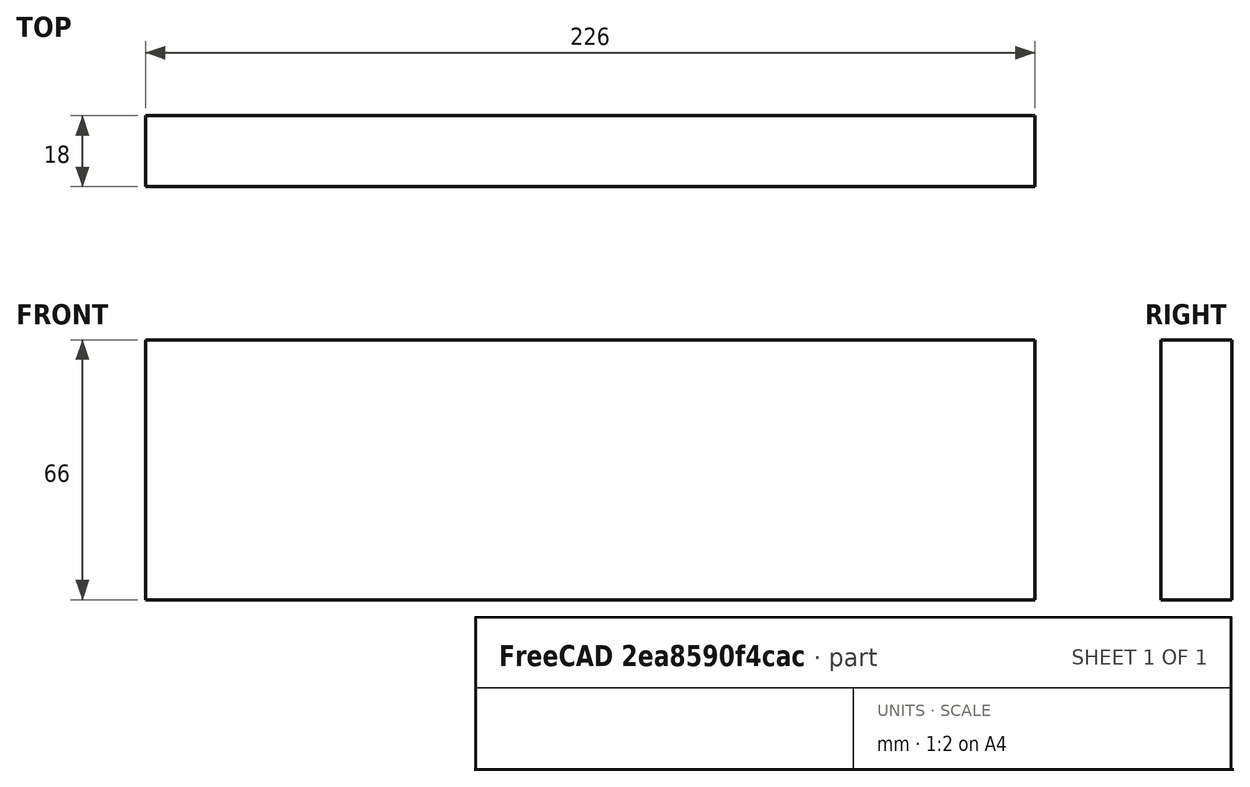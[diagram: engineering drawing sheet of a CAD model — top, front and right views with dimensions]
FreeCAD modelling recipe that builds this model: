
FCSTD DOCUMENT  (FreeCAD 0.18R4 (GitTag))
Label: drawer_front
License: All rights reserved
LicenseURL: http://en.wikipedia.org/wiki/All_rights_reserved
objects: Sketcher::SketchObject×1, PartDesign::Pad×1, PartDesign::Body×1
note: 4 computed .brp shape members not serialized (recipe doc carries the construction recipe); baked Part::Feature solids carry a one-line shape summary decoded from their .brp

FEATURE [Sketcher::SketchObject] Sketch
  MapMode = 5
  Placement = pos=(0,0,0) rot=(1,0,0;1.5708rad)
  Support = -> [XZ_Plane]
  sketch-geometry (4):
    g0: LineSegment StartX=0 StartY=0 StartZ=0 EndX=-226 EndY=0 EndZ=0
    g1: LineSegment StartX=-226 StartY=0 StartZ=0 EndX=-226 EndY=66 EndZ=0
    g2: LineSegment StartX=-226 StartY=66 StartZ=0 EndX=0 EndY=66 EndZ=0
    g3: LineSegment StartX=0 StartY=66 StartZ=0 EndX=0 EndY=0 EndZ=0
  constraints (11):
    c: Coincident(g0,g1)
    c: Coincident(g1,g2)
    c: Coincident(g2,g3)
    c: Coincident(g3,g0)
    c: Horizontal(g0)
    c: Horizontal(g2)
    c: Vertical(g1)
    c: Vertical(g3)
    c: Coincident(g0,g-1)
    c: DistanceX(g0,g0) = 226
    c: DistanceY(g3,g3) = 66
FEATURE [PartDesign::Pad] Pad
  Length = 18
  Length2 = 100
  Placement = pos=(0,0,0) rot=(1,0,0;1.5708rad)
  Profile = -> Sketch
  Type = 0
FEATURE [PartDesign::Body] Body
  Group = -> [Sketch,Pad]
  Origin = -> Origin
  Tip = -> Pad
